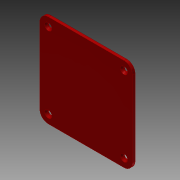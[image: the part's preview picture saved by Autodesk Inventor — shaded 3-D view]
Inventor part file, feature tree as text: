
AUTODESK INVENTOR PART (.ipt)
format: ipt  version: 2015 (Build 190159000, 159)  size: 120,832 bytes
history: native  units: in
note: dims shown in document units (in); Inventor stores cm internally (conversion verified against a paired STEP export)
features: sketch x3, extrude x2, hole x1, chamfer x1, fillet x1
ambient origin geometry x8: Origin, YZ Plane, XZ Plane, XY Plane, X Axis, Y Axis, Z Axis, Center Point
bodies: Solid1 (feature_tree)
feature tree (8):
  extrude  "Extrusion1"  Depth=2.75in
  hole  "Hole1"  [1 undecoded]
  extrude  "Extrusion2"  Depth=0.05in
  chamfer  "Chamfer1"  Distance=1.15in
  fillet  "Fillet1"  Radius=0.5in
  sketch  "Sketch1"  dims[d0=2.75in d1=2.75in]
  sketch  "Sketch2"  dims[d2=0.25in d3=0.08in d4=0.0in]
  sketch  "Sketch3"  dims[d5=0.126in d6=0.75in d7=0.2205in d8=0.25in d9=90.0deg d10=1.0in d11=0.8108in d12=0.1181in d13=1.15in d14=0.5in d15=0.575in d16=0.15in d17=0.0in d18=0.02in d19=0.125in d20=30.0deg d21=0.05in]
note: 1 required parameter value undecoded (feature->parameter linkage not recoverable at this tier; creation-order binding heuristic only, values carry confidence <= 0.55)
